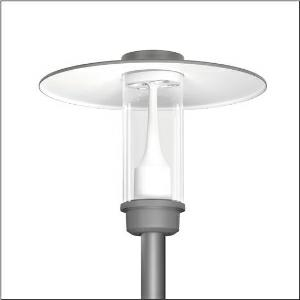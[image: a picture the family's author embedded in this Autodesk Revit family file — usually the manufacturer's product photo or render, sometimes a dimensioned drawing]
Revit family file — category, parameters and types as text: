
# Revit family: litepole_2_iq___p1_0a_5xa5425ff14h000022_e316
name_source: partatom
category: Lighting Fixtures
units: mm (PartAtom-declared; Revit-internal decimal feet)

## family parameters
Cut with Voids When Loaded = No
Host = Face
Light Source = No
Part Type = Normal
Room Calculation Point = No
Round Connector Dimension = Use Diameter
Shared = No

## types (1)
- --- (1 x LED, 1520 lm, 10.5 W, 3000K)
    Apparent Load = 11 VA
    CIE Flux Codes = 33 62 89 96 100
    Color Rendering = 70
    Color Temperature = 3000K
    Default Elevation = 1800 mm
    Description = Litepole 2 iQ, mast luminaire, Module 540 iQ-SR, primary light control with 3 zone facetted reflector, of plastic, silver coated, highly specular, structured, primary optical cover: cover, of PMMA, transparent, light distribution: P1.0a, light emission: direct distribution, primary light characteristic: strongly asymmetric, installation type: post-top, LED, High Power LED, rated luminous flux: 1.520lm, luminous efficacy: 145lm/W, light colour: 730, colour temperature: 3000K, control gear: iQ Street-Remote, control: Street-Remote, Auto-Match, Temp-Guard, Lumen-Switch, Night-Set, Smart-Wire, Light-Fading, Desk-Remote (wireless, voltage-free reading and setting of iQ features in the workshop via application-optimized NFC function/RFID function), optimised constant luminous flux control (CLO 2.0), pre-setting: logarithmic dimming characteristic, mains connection: 230..240V, AC, 50/60Hz, connection cable pre-assembled, cable length: 5,5m, wiring characteristics: H07RN-F, start of lifetime: 11W, end of service life: 11W, reduction: 5W, luminaire housing, upper part, of aluminium, coated, Siteco® metallic grey (DB 702S), diameter: 750mm, height: 590mm, spigot size: d x l = 76 x 70mm (post-top) | with reducer (optional accessory) 60 x 70mm, mounting height: 3..5m, post-top mast mounting element, of diecast aluminium, coated, Siteco® metallic grey (DB 702S), Module 540 iQ-SR, traffic white (RAL 9016), equipment: standard, protection rating (complete): IP65, insulation class (complete): insulation class II (safety insulation), certification: CE, ENEC, VDE, packaging unit: 1 piece

Light Distribution: P1.0a
    Height = 590 mm
    Lamp = 1 x LED
    Lamp Light Flux = 1520 lm
    Lamp Power = 10.5 W
    Lamp count = 1
    Length = 750 mm
    Luminous efficacy = 145 lm/W
    Manufacturer = Siteco
    ModVariant = No
    Model = 5XA5425FF14H000022
    Number of Poles = 1
    OnlyDefault = Yes
    Power Factor = 1
    Product Name = Litepole 2 iQ | P1.0a
    Product group = mast luminaire | pylon top
    ProductGroupID = 6100
    Protection Class = Protection class II
    Protection Degree = IP 65
    RLX_Detail_Level = 1
    RLX_Emergency_Light_Flux = 0 lm
    RLX_Emergency_Type = 0
    RLX_Emergency_Type_DB = No
    RlxData = <blob elided: 31137 chars, md5=43a7ed25>
    Socket = socket
    Standby Power = 0 W
    System Light Flux = 1520 lm
    System Power = 11 W
    Type Comments = factory setting: luminous flux: 100 % | dim-lin: 254 | 419 mA
    Type Image = l_1006518.jpg
    URL = http://relux.com
    VarID = @adj_213749
    Voltage = 0 V
    Weight = 0.00 kg
    Width = 0 mm  [stored 0 ft]

note: [stored X ft] marks values corroborated as IEEE doubles in the binary element streams (Revit-internal decimal feet)

## geometry (parser evidence)
native form markers: Blend x4, Sweep x9
no freeform markers — native parametric forms only
